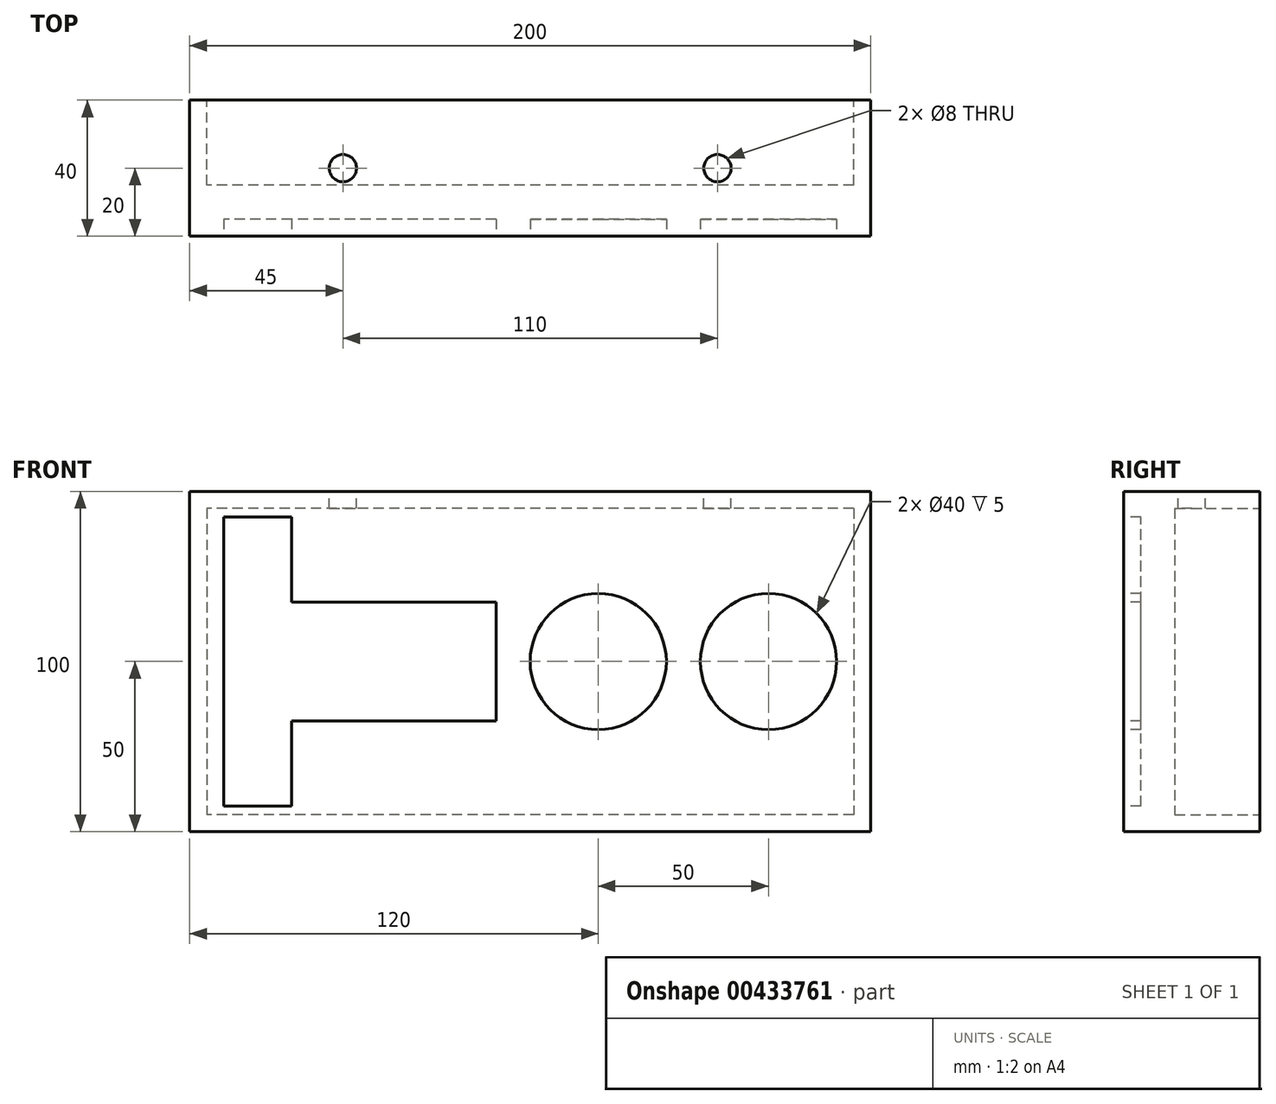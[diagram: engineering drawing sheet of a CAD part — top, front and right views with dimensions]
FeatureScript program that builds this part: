
annotation { "Feature Type Name" : "Feature", "Feature Type Description" : "" }
export const myFeature = defineFeature(function(context is Context, id is Id, definition is map)
    precondition{}
    {
        {
            var Q0;
            Q0=qCreatedBy(makeId("Front.planeOp"),FACE);
            var sketch = newSketch(context, id + "F0", { "sketchPlane" : qUnion([Q0])});
            skLineSegment(sketch, "E0.bottom", {"start": v(100, -50) * mm, "end": v(-100, -50) * mm});
            skLineSegment(sketch, "E0.top", {"start": v(100, 50) * mm, "end": v(-100, 50) * mm});
            skLineSegment(sketch, "E0.left", {"start": v(100, -50) * mm, "end": v(100, 50) * mm});
            skLineSegment(sketch, "E0.right", {"start": v(-100, -50) * mm, "end": v(-100, 50) * mm});
            skPoint(sketch, "E0.middle", {"position": v(0, 0) * mm});
            skSolve(sketch);
        }
        {
            var Q0;
            Q0=makeQuery(id+"F0.imprint","IMPRINT",FACE,{"disambiguationData":[TD([[makeQuery(id+"F0.imprint","IMPRINT",EDGE,{"derivedFrom":sQuery(id+"F0.wireOp",EDGE,"E0.bottom")}),-1.0]])]});
            extrude(context, id + "F1", {"entities" : qUnion([Q0]), "depth" : 40 * mm});
        }
        {
            var Q0;
            Q0=makeQuery(id+"F1.opExtrude","CAP_FACE",FACE,{"disambiguationData":[OSD([sQuery(id+"F0.wireOp",EDGE,"E0.bottom"),sQuery(id+"F0.wireOp",EDGE,"E0.top"),sQuery(id+"F0.wireOp",EDGE,"E0.left"),sQuery(id+"F0.wireOp",EDGE,"E0.right")])],"isStart":false});
            var sketch = newSketch(context, id + "F2", { "sketchPlane" : qUnion([Q0])});
            skCircle(sketch, "E1", {"center": v(70, 0) * mm, "radius": 20 * mm});
            skCircle(sketch, "E2", {"center": v(20, 0) * mm, "radius": 20 * mm});
            skLineSegment(sketch, "E3.bottom", {"start": v(-70, -42.5) * mm, "end": v(-90, -42.5) * mm});
            skLineSegment(sketch, "E3.top", {"start": v(-70, 42.5) * mm, "end": v(-90, 42.5) * mm});
            skLineSegment(sketch, "E3.left", {"start": v(-70, -42.5) * mm, "end": v(-70, 42.5) * mm});
            skLineSegment(sketch, "E3.right", {"start": v(-90, -42.5) * mm, "end": v(-90, 42.5) * mm});
            skPoint(sketch, "E3.middle", {"position": v(-80, 0) * mm});
            skLineSegment(sketch, "E4.bottom", {"start": v(-10, -17.5) * mm, "end": v(-70, -17.5) * mm});
            skLineSegment(sketch, "E4.top", {"start": v(-10, 17.5) * mm, "end": v(-70, 17.5) * mm});
            skLineSegment(sketch, "E4.left", {"start": v(-10, -17.5) * mm, "end": v(-10, 17.5) * mm});
            skLineSegment(sketch, "E4.right", {"start": v(-70, -17.5) * mm, "end": v(-70, 17.5) * mm});
            skPoint(sketch, "E4.middle", {"position": v(-40, 0) * mm});
            skSolve(sketch);
        }
        {
            var Q0;
            {var subQ3=sQuery(id+"F2.wireOp",EDGE,"E3.bottom");Q0=makeQuery(id+"F2.imprint","IMPRINT",FACE,{"disambiguationData":[TD([[makeQuery(id+"F2.imprint","IMPRINT",EDGE,{"derivedFrom":subQ3}),-1.0]])]});}
            var Q1;
            Q1=makeQuery(id+"F2.imprint","IMPRINT",FACE,{"disambiguationData":[TD([[makeQuery(id+"F2.imprint","IMPRINT",EDGE,{"derivedFrom":sQuery(id+"F2.wireOp",EDGE,"E4.bottom")}),-1.0]])]});
            var Q2;
            Q2=makeQuery(id+"F2.imprint","IMPRINT",FACE,{"disambiguationData":[TD([[makeQuery(id+"F2.imprint","IMPRINT",EDGE,{"derivedFrom":sQuery(id+"F2.wireOp",EDGE,"E2")}),1.0]])]});
            var Q3;
            Q3=makeQuery(id+"F2.imprint","IMPRINT",FACE,{"disambiguationData":[TD([[makeQuery(id+"F2.imprint","IMPRINT",EDGE,{"derivedFrom":sQuery(id+"F2.wireOp",EDGE,"E1")}),1.0]])]});
            extrude(context, id + "F3", {"entities" : qUnion([Q0, Q1, Q2, Q3]), "operationType" : NewBodyOperationType.REMOVE, "oppositeDirection" : true, "depth" : 5 * mm});
        }
        {
            var Q0;
            Q0=makeQuery(id+"F1.opExtrude","CAP_FACE",FACE,{"disambiguationData":[OSD([sQuery(id+"F0.wireOp",EDGE,"E0.bottom"),sQuery(id+"F0.wireOp",EDGE,"E0.top"),sQuery(id+"F0.wireOp",EDGE,"E0.left"),sQuery(id+"F0.wireOp",EDGE,"E0.right")])],"isStart":true});
            var sketch = newSketch(context, id + "F4", { "sketchPlane" : qUnion([Q0])});
            skLineSegment(sketch, "E5.bottom", {"start": v(-95, 45) * mm, "end": v(95, 45) * mm});
            skLineSegment(sketch, "E5.top", {"start": v(-95, -45) * mm, "end": v(95, -45) * mm});
            skLineSegment(sketch, "E5.left", {"start": v(-95, 45) * mm, "end": v(-95, -45) * mm});
            skLineSegment(sketch, "E5.right", {"start": v(95, 45) * mm, "end": v(95, -45) * mm});
            skPoint(sketch, "E5.middle", {"position": v(0, 0) * mm});
            skSolve(sketch);
        }
        {
            var Q0;
            Q0=makeQuery(id+"F4.imprint","IMPRINT",FACE,{"disambiguationData":[TD([[makeQuery(id+"F4.imprint","IMPRINT",EDGE,{"derivedFrom":sQuery(id+"F4.wireOp",EDGE,"E5.bottom")}),-1.0]])]});
            extrude(context, id + "F5", {"entities" : qUnion([Q0]), "operationType" : NewBodyOperationType.REMOVE, "oppositeDirection" : true, "depth" : 25 * mm});
        }
        {
            var Q0;
            Q0=makeQuery(id+"F1.opExtrude","SWEPT_FACE",FACE,{"disambiguationData":[OSD([sQuery(id+"F0.wireOp",EDGE,"E0.top")])]});
            var sketch = newSketch(context, id + "F6", { "sketchPlane" : qUnion([Q0])});
            skCircle(sketch, "E6", {"center": v(-55, -20) * mm, "radius": 4 * mm});
            skCircle(sketch, "E7", {"center": v(55, -20) * mm, "radius": 4 * mm});
            skSolve(sketch);
        }
        {
            var Q0;
            Q0 = qSketchRegion(id + "F6", true);
            extrude(context, id + "F7", {"entities" : qUnion([Q0]), "operationType" : NewBodyOperationType.REMOVE, "oppositeDirection" : true, "depth" : 40 * mm});
        }
    });
